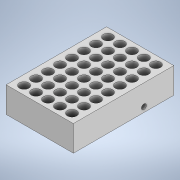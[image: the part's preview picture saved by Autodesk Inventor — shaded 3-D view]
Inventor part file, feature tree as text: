
AUTODESK INVENTOR PART (.ipt)
format: ipt  version: 2020 (Build 240168000, 168)  size: 228,864 bytes
history: native  units: in
note: dims shown in document units (in); Inventor stores cm internally (conversion verified against a paired STEP export)
features: sketch x6, hole x5, extrude x1, pattern_linear x1
ambient origin geometry x8: Origin, YZ Plane, XZ Plane, XY Plane, X Axis, Y Axis, Z Axis, Center Point
bodies: Solid1 (feature_tree)
feature tree (13):
  extrude  "Extrusion1"  Depth=5.0299in
  hole  "Hole1"  [1 undecoded]
  hole  "Hole2"  [1 undecoded]
  pattern_linear  "Rectangular Pattern1"  Spacing1=1.2874in  [1 undecoded]
  hole  "Hole3"  [1 undecoded]
  hole  "Hole4"  [1 undecoded]
  hole  "Hole5"  [1 undecoded]
  sketch  "Sketch1"  dims[d0=3.3654in d1=5.0299in]
  sketch  "Sketch2"  dims[d2=1.0in d3=135.0deg]
  sketch  "Sketch4"  dims[d4=1.0in d5=1.0in]
  sketch  "Sketch5"  dims[d6=135.0deg]
  sketch  "Sketch6"  dims[d7=1.0in]
  sketch  "Sketch7"  dims[d8=45.0deg d9=1.2874in d10=0.0in d11=1.0in d12=135.0deg d13=1.0in d14=135.0deg d15=1.0in d16=45.0deg d17=1.0in d18=45.0deg d19=0.145in d20=0.25in d21=0.375in d22=0.19in d23=0.5635in d24=0.375in d25=0.8108in d28=0.4724in d29=0.25in d30=0.375in d31=0.25in d32=0.5635in d33=0.7874in d34=0.0in d35=1.9685in d37=0.6in d38=3.1496in d40=0.6in d41=0.483in d42=0.415in d43=1.5in d44=0.25in d45=0.25in d46=0.25in d47=0.119in d48=0.25in d49=0.5635in d50=1.25in d51=0.8108in d52=0.25in d53=0.125in d54=0.25in d55=0.119in d56=0.25in d57=0.5635in d58=2.0in d59=0.8108in d60=1.5in d61=0.25in d62=0.25in d63=0.25in d64=0.119in d65=0.25in d66=0.5635in d67=1.25in d68=0.8108in]
note: 6 required parameter values undecoded (feature->parameter linkage not recoverable at this tier; creation-order binding heuristic only, values carry confidence <= 0.55)
